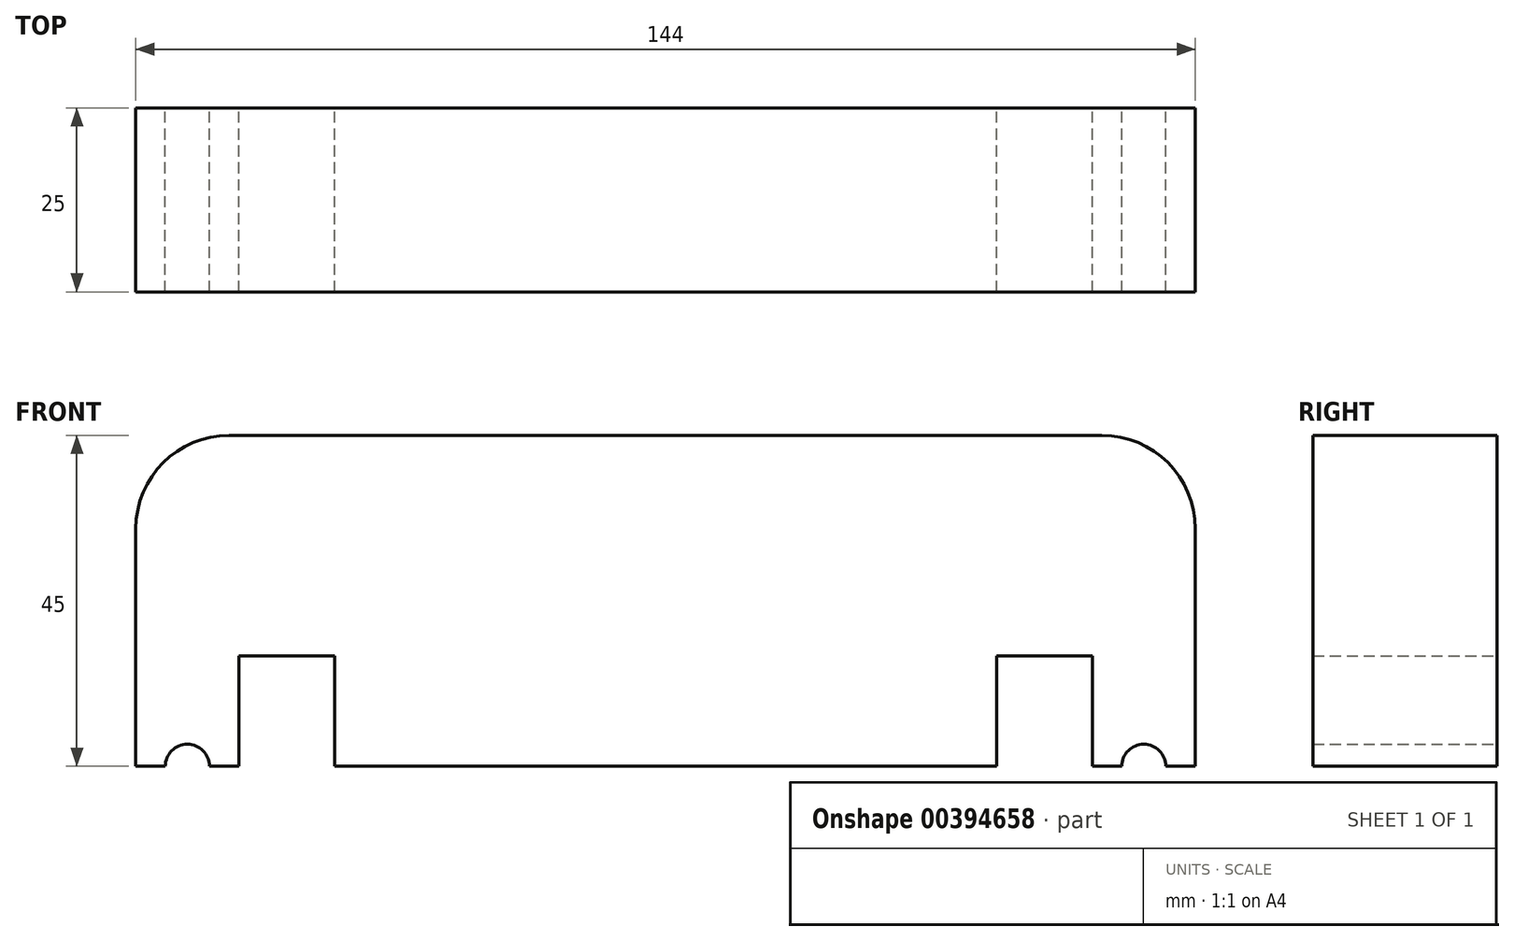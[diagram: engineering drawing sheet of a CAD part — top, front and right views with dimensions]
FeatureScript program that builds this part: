
annotation { "Feature Type Name" : "Feature", "Feature Type Description" : "" }
export const myFeature = defineFeature(function(context is Context, id is Id, definition is map)
    precondition{}
    {
        {
            var Q0;
            Q0=qCreatedBy(makeId("Front.planeOp"),FACE);
            var sketch = newSketch(context, id + "F0", { "sketchPlane" : qUnion([Q0])});
            skLineSegment(sketch, "E0.bottom", {"start": v(59.3, 22.5) * mm, "end": v(-59.3, 22.5) * mm});
            skLineSegment(sketch, "E0.left", {"start": v(72, 9.8) * mm, "end": v(72, -22.5) * mm});
            skLineSegment(sketch, "E0.right", {"start": v(-72, 9.8) * mm, "end": v(-72, -22.5) * mm});
            skPoint(sketch, "E0.middle", {"position": v(0, 0) * mm});
            skLineSegment(sketch, "E1.top", {"start": v(-58, -7.5) * mm, "end": v(-45, -7.5) * mm});
            skLineSegment(sketch, "E1.left", {"start": v(-58, -22.5) * mm, "end": v(-58, -7.5) * mm});
            skLineSegment(sketch, "E1.right", {"start": v(-45, -22.5) * mm, "end": v(-45, -7.5) * mm});
            skLineSegment(sketch, "E2.top", {"start": v(45, -7.5) * mm, "end": v(58, -7.5) * mm});
            skLineSegment(sketch, "E2.left", {"start": v(45, -22.5) * mm, "end": v(45, -7.5) * mm});
            skLineSegment(sketch, "E2.right", {"start": v(58, -22.5) * mm, "end": v(58, -7.5) * mm});
            skPoint(sketch, "E3.visualSharp", {"position": v(-72, -22.5) * mm});
            skPoint(sketch, "E4.visualSharp", {"position": v(72, -22.5) * mm});
            skPoint(sketch, "E5.visualSharp", {"position": v(-72, 22.5) * mm});
            skArc(sketch, "E5.filletArc", {"start": v(-59.3, 22.5) * mm, "mid": v(-68.28, 18.78) * mm, "end": v(-72, 9.8) * mm});
            skPoint(sketch, "E6.visualSharp", {"position": v(72, 22.5) * mm});
            skArc(sketch, "E6.filletArc", {"start": v(72, 9.8) * mm, "mid": v(68.28, 18.78) * mm, "end": v(59.3, 22.5) * mm});
            skLineSegment(sketch, "E7.trimOffspring", {"start": v(-58, -22.5) * mm, "end": v(-62, -22.5) * mm});
            skLineSegment(sketch, "E8.trimOffspring", {"start": v(45, -22.5) * mm, "end": v(-45, -22.5) * mm});
            skArc(sketch, "E9", {"start": v(-68, -22.5) * mm, "mid": v(-65, -19.5) * mm, "end": v(-62, -22.5) * mm});
            skLineSegment(sketch, "E10.trimOffspring", {"start": v(-68, -22.5) * mm, "end": v(-72, -22.5) * mm});
            skLineSegment(sketch, "E11", {"start": v(58, -22.5) * mm, "end": v(62, -22.5) * mm});
            skArc(sketch, "E12", {"start": v(62, -22.5) * mm, "mid": v(65, -19.5) * mm, "end": v(68, -22.5) * mm});
            skLineSegment(sketch, "E13.trimOffspring", {"start": v(68, -22.5) * mm, "end": v(72, -22.5) * mm});
            skSolve(sketch);
        }
        {
            var Q0;
            Q0=makeQuery(id+"F0.imprint","IMPRINT",FACE,{"disambiguationData":[TD([[makeQuery(id+"F0.imprint","IMPRINT",EDGE,{"derivedFrom":sQuery(id+"F0.wireOp",EDGE,"E0.bottom")}),1.0]])]});
            extrude(context, id + "F1", {"entities" : qUnion([Q0]), "depth" : 25 * mm, "offsetDistance" : 25 * mm});
        }
    });
